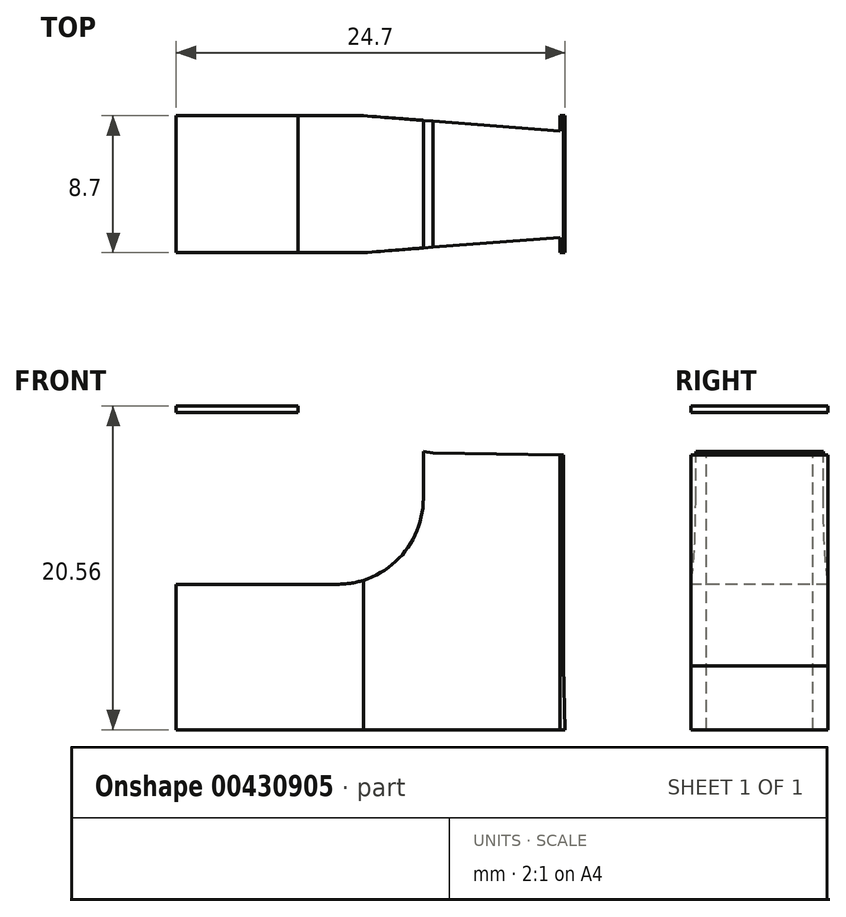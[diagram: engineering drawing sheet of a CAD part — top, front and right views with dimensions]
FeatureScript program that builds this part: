
annotation { "Feature Type Name" : "Feature", "Feature Type Description" : "" }
export const myFeature = defineFeature(function(context is Context, id is Id, definition is map)
    precondition{}
    {
        {
            var Q0;
            Q0=qCreatedBy(makeId("Front.planeOp"),FACE);
            var sketch = newSketch(context, id + "F0", { "sketchPlane" : qUnion([Q0])});
            skLineSegment(sketch, "E0", {"start": v(-31.43, 0) * mm, "end": v(-31.43, 13.4) * mm});
            skPoint(sketch, "E1.endSnap0", {"position": v(-44.03, 0) * mm});
            skLineSegment(sketch, "E2", {"start": v(-48.29, 16.5) * mm, "end": v(-56.03, 16.5) * mm});
            skLineSegment(sketch, "E3", {"start": v(-56.03, 16.5) * mm, "end": v(-56.03, 0) * mm});
            skLineSegment(sketch, "E4", {"start": v(-48.27, 14.9) * mm, "end": v(-39.71, 13.53) * mm});
            skLineSegment(sketch, "E5", {"start": v(-56.03, 0) * mm, "end": v(-56.03, -4.06) * mm});
            skLineSegment(sketch, "E6", {"start": v(-56.03, -4.06) * mm, "end": v(-31.33, -4.06) * mm});
            skLineSegment(sketch, "E7", {"start": v(-31.43, 0) * mm, "end": v(-31.33, -4.06) * mm});
            skLineSegment(sketch, "E8", {"start": v(-39.71, 13.53) * mm, "end": v(-31.43, 13.4) * mm});
            skLineSegment(sketch, "E9", {"start": v(-48.29, 16.5) * mm, "end": v(-48.27, 14.9) * mm});
            skSolve(sketch);
        }
        {
            var Q0;
            Q0=qCreatedBy(makeId("Front.planeOp"),FACE);
            var sketch = newSketch(context, id + "F1", { "sketchPlane" : qUnion([Q0])});
            skLineSegment(sketch, "E10.bottom", {"start": v(-56.28, 16.09) * mm, "end": v(-45.78, 16.09) * mm});
            skLineSegment(sketch, "E10.top", {"start": v(-56.28, 5.19) * mm, "end": v(-45.78, 5.19) * mm});
            skLineSegment(sketch, "E10.left", {"start": v(-56.28, 16.09) * mm, "end": v(-56.28, 5.19) * mm});
            skPoint(sketch, "E11", {"position": v(-56.48, 10.64) * mm});
            skArc(sketch, "E12", {"start": v(-45.78, 5.19) * mm, "mid": v(-40.33, 10.64) * mm, "end": v(-45.78, 16.09) * mm});
            skLineSegment(sketch, "E13", {"start": v(-45.78, 16.09) * mm, "end": v(-40.33, 16.09) * mm});
            skPoint(sketch, "E13.endSnap0", {"position": v(-40.33, 10.64) * mm});
            skLineSegment(sketch, "E14", {"start": v(-40.33, 16.09) * mm, "end": v(-40.33, 10.64) * mm});
            skSolve(sketch);
        }
        {
            var Q0;
            Q0 = qSketchRegion(id + "F0", true);
            var Q1;
            Q1 = qSketchRegion(id + "F1", true);
            extrude(context, id + "F2", {"entities" : qUnion([Q0, Q1]), "endBound" : BoundingType.SYMMETRIC, "depth" : 8.7 * mm});
        }
        {
            var Q0;
            Q0=qCreatedBy(makeId("Top.planeOp"),FACE);
            var sketch = newSketch(context, id + "F3", { "sketchPlane" : qUnion([Q0])});
            skLineSegment(sketch, "E15", {"start": v(-45.21, -4.43) * mm, "end": v(-31.66, -3.38) * mm});
            skLineSegment(sketch, "E16", {"start": v(-31.66, -3.38) * mm, "end": v(-31.66, -4.46) * mm});
            skLineSegment(sketch, "E17", {"start": v(-31.66, -4.46) * mm, "end": v(-45.21, -4.43) * mm});
            skLineSegment(sketch, "E18.MirrorCS", {"start": v(-45.21, 4.43) * mm, "end": v(-31.66, 3.38) * mm});
            skLineSegment(sketch, "E19.MirrorCS", {"start": v(-31.66, 4.46) * mm, "end": v(-45.21, 4.43) * mm});
            skLineSegment(sketch, "E20.MirrorCS", {"start": v(-31.66, 3.38) * mm, "end": v(-31.66, 4.46) * mm});
            skSolve(sketch);
        }
        {
            var Q0;
            Q0 = qSketchRegion(id + "F3", true);
            extrude(context, id + "F4", {"entities" : qUnion([Q0]), "operationType" : NewBodyOperationType.REMOVE, "endBound" : BoundingType.SYMMETRIC, "oppositeDirection" : true, "depth" : 27.5 * mm, "hasSecondDirection" : true, "secondDirectionOppositeDirection" : true, "secondDirectionDepth" : 25 * mm});
        }
        {
            var Q0;
            Q0 = qSketchRegion(id + "F1", true);
            var Q1;
            Q1 = qConstructionFilter(qBodyType(qCreatedBy(id + "F1" ,EDGE), BodyType.WIRE), ConstructionObject.NO);
            extrude(context, id + "F5", {"entities" : qUnion([Q0]), "operationType" : NewBodyOperationType.REMOVE, "surfaceEntities" : qUnion([Q1]), "endBound" : BoundingType.SYMMETRIC, "depth" : 21 * mm});
        }
    });
